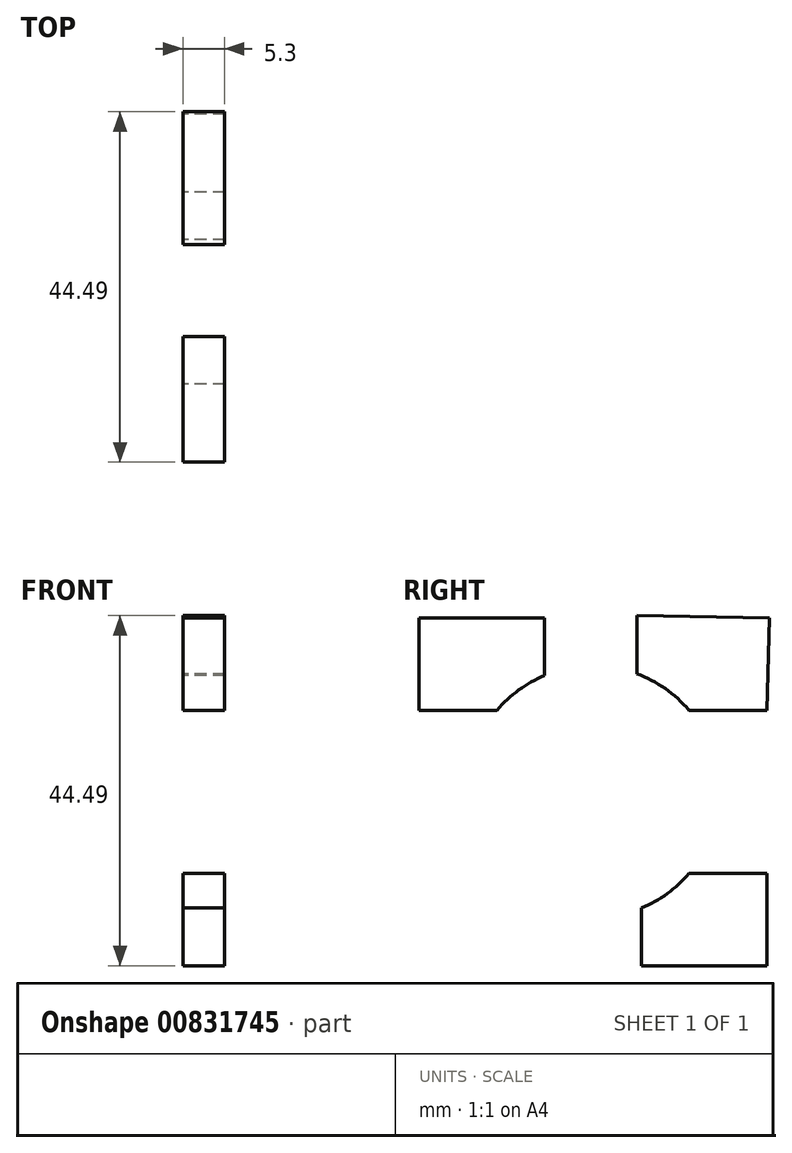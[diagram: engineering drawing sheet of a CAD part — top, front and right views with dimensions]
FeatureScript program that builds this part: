
annotation { "Feature Type Name" : "Feature", "Feature Type Description" : "" }
export const myFeature = defineFeature(function(context is Context, id is Id, definition is map)
    precondition{}
    {
        {
            var Q0;
            Q0=qCreatedBy(makeId("Right.planeOp"),FACE);
            var sketch = newSketch(context, id + "F0", { "sketchPlane" : qUnion([Q0])});
            skCircle(sketch, "E0", {"center": v(1, -0.14) * mm, "radius": 16 * mm});
            skLineSegment(sketch, "E1.top", {"start": v(-21.09, -22.53) * mm, "end": v(23.4, -22.53) * mm});
            skLineSegment(sketch, "E2.bottom", {"start": v(-21.09, 10.23) * mm, "end": v(-5.16, 10.23) * mm});
            skLineSegment(sketch, "E2.top", {"start": v(-21.09, 21.96) * mm, "end": v(-5.16, 21.96) * mm});
            skLineSegment(sketch, "E2.left", {"start": v(-21.09, 10.23) * mm, "end": v(-21.09, 21.96) * mm});
            skLineSegment(sketch, "E2.right", {"start": v(-5.16, 10.23) * mm, "end": v(-5.16, 21.96) * mm});
            skLineSegment(sketch, "E3.1.0", {"start": v(23.1, -10.5) * mm, "end": v(23.1, -22.23) * mm});
            skLineSegment(sketch, "E3.1.1", {"start": v(23.1, -10.5) * mm, "end": v(7.17, -10.5) * mm});
            skLineSegment(sketch, "E3.1.2", {"start": v(7.17, -10.5) * mm, "end": v(7.17, -22.23) * mm});
            skLineSegment(sketch, "E3.1.3", {"start": v(23.1, -22.23) * mm, "end": v(7.17, -22.23) * mm});
            skLineSegment(sketch, "E4.bottom", {"start": v(-21.09, -10.5) * mm, "end": v(-4.56, -10.5) * mm});
            skLineSegment(sketch, "E4.top", {"start": v(-21.09, -22.53) * mm, "end": v(-4.56, -22.53) * mm});
            skLineSegment(sketch, "E4.left", {"start": v(-21.09, -10.5) * mm, "end": v(-21.09, -22.53) * mm});
            skLineSegment(sketch, "E4.right", {"start": v(-4.56, -10.5) * mm, "end": v(-4.56, -22.53) * mm});
            skLineSegment(sketch, "E5.1.0", {"start": v(23.1, 10.23) * mm, "end": v(6.56, 10.23) * mm});
            skLineSegment(sketch, "E5.1.1", {"start": v(6.56, 10.23) * mm, "end": v(6.56, 22.26) * mm});
            skLineSegment(sketch, "E5.1.2", {"start": v(23.1, 22.26) * mm, "end": v(6.56, 22.26) * mm});
            skLineSegment(sketch, "E6", {"start": v(23.4, 21.96) * mm, "end": v(23.1, 10.23) * mm});
            skLineSegment(sketch, "E7", {"start": v(23.4, 21.96) * mm, "end": v(6.56, 22.26) * mm});
            skSolve(sketch);
        }
        {
            var Q0;
            {var subQ4=sQuery(id+"F0.wireOp",EDGE,"E6");Q0=makeQuery(id+"F0.imprint","IMPRINT",FACE,{"disambiguationData":[TD([[makeQuery(id+"F0.imprint","IMPRINT",EDGE,{"derivedFrom":subQ4}),-1.0]])]});}
            var Q1;
            {var subQ1=sQuery(id+"F0.wireOp",EDGE,"E2.top");Q1=makeQuery(id+"F0.imprint","IMPRINT",FACE,{"disambiguationData":[TD([[makeQuery(id+"F0.imprint","IMPRINT",EDGE,{"derivedFrom":subQ1}),-1.0]])]});}
            var Q2;
            {var subQ5=sQuery(id+"F0.wireOp",EDGE,"E3.1.0");Q2=makeQuery(id+"F0.imprint","IMPRINT",FACE,{"disambiguationData":[TD([[makeQuery(id+"F0.imprint","IMPRINT",EDGE,{"derivedFrom":subQ5}),-1.0]])]});}
            var Q3;
            {var subQ1=sQuery(id+"F0.wireOp",EDGE,"E4.top");Q3=makeQuery(id+"F0.imprint","IMPRINT",FACE,{"disambiguationData":[TD([[makeQuery(id+"F0.imprint","IMPRINT",EDGE,{"derivedFrom":subQ1}),1.0]])]});}
            extrude(context, id + "F1", {"entities" : qUnion([Q0, Q1, Q2, Q3]), "depth" : 5.3 * mm, "offsetDistance" : 25 * mm});
        }
    });
